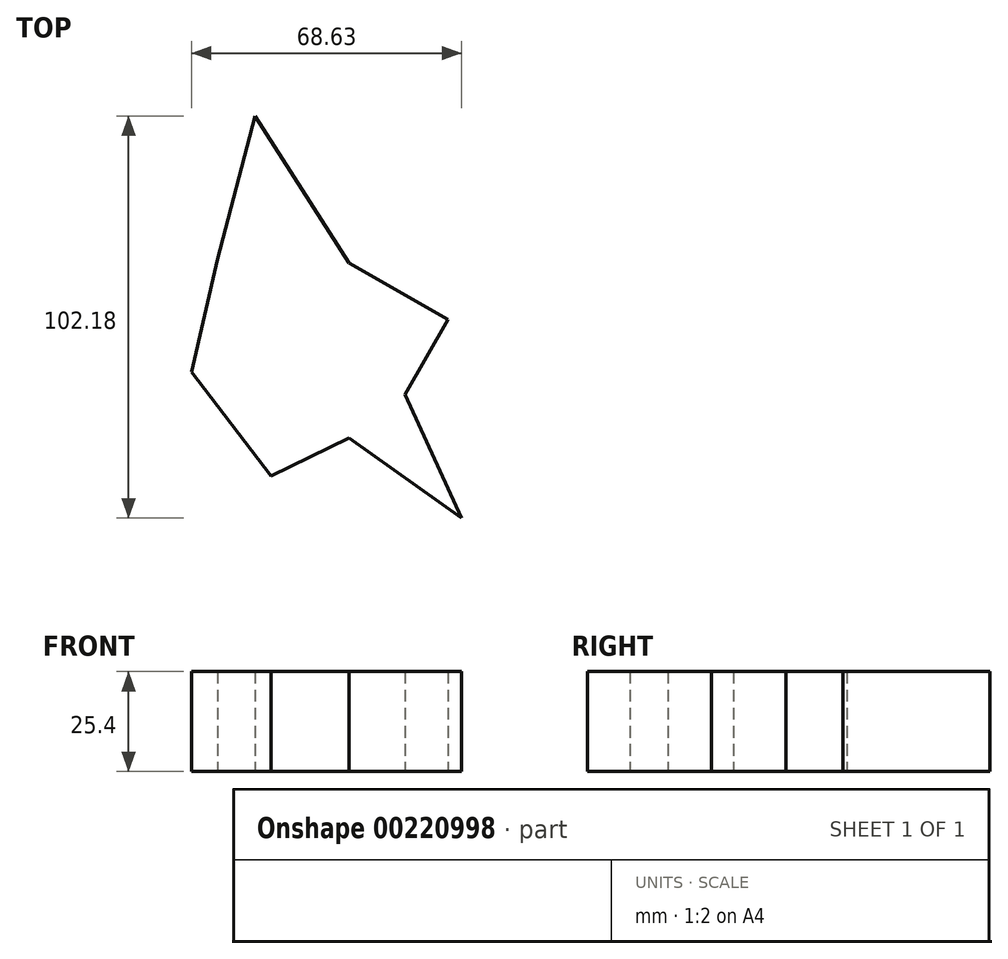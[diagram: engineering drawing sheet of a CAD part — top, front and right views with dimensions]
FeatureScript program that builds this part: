
annotation { "Feature Type Name" : "Feature", "Feature Type Description" : "" }
export const myFeature = defineFeature(function(context is Context, id is Id, definition is map)
    precondition{}
    {
        {
            var Q0;
            Q0=qCreatedBy(makeId("Top.planeOp"),FACE);
            var sketch = newSketch(context, id + "F0", { "sketchPlane" : qUnion([Q0])});
            skLineSegment(sketch, "E0", {"start": v(-65.8, 106.6) * mm, "end": v(-56.28, 142.91) * mm});
            skLineSegment(sketch, "E1", {"start": v(-56.28, 142.91) * mm, "end": v(-32.41, 105.55) * mm});
            skLineSegment(sketch, "E2", {"start": v(-32.41, 105.55) * mm, "end": v(-7.38, 91.15) * mm});
            skLineSegment(sketch, "E3", {"start": v(-7.38, 91.15) * mm, "end": v(-18.3, 72.16) * mm});
            skLineSegment(sketch, "E4", {"start": v(-18.3, 72.16) * mm, "end": v(-3.84, 40.73) * mm});
            skLineSegment(sketch, "E5", {"start": v(-3.84, 40.73) * mm, "end": v(-32.41, 61.1) * mm});
            skLineSegment(sketch, "E6", {"start": v(-32.41, 61.1) * mm, "end": v(-52.32, 51.43) * mm});
            skLineSegment(sketch, "E7", {"start": v(-52.32, 51.43) * mm, "end": v(-72.47, 77.83) * mm});
            skLineSegment(sketch, "E8", {"start": v(-72.47, 77.83) * mm, "end": v(-65.8, 106.6) * mm});
            skSolve(sketch);
        }
        {
            var Q0;
            Q0 = qSketchRegion(id + "F0", true);
            extrude(context, id + "F1", {"entities" : qUnion([Q0]), "depth" : 25.4 * mm});
        }
    });
